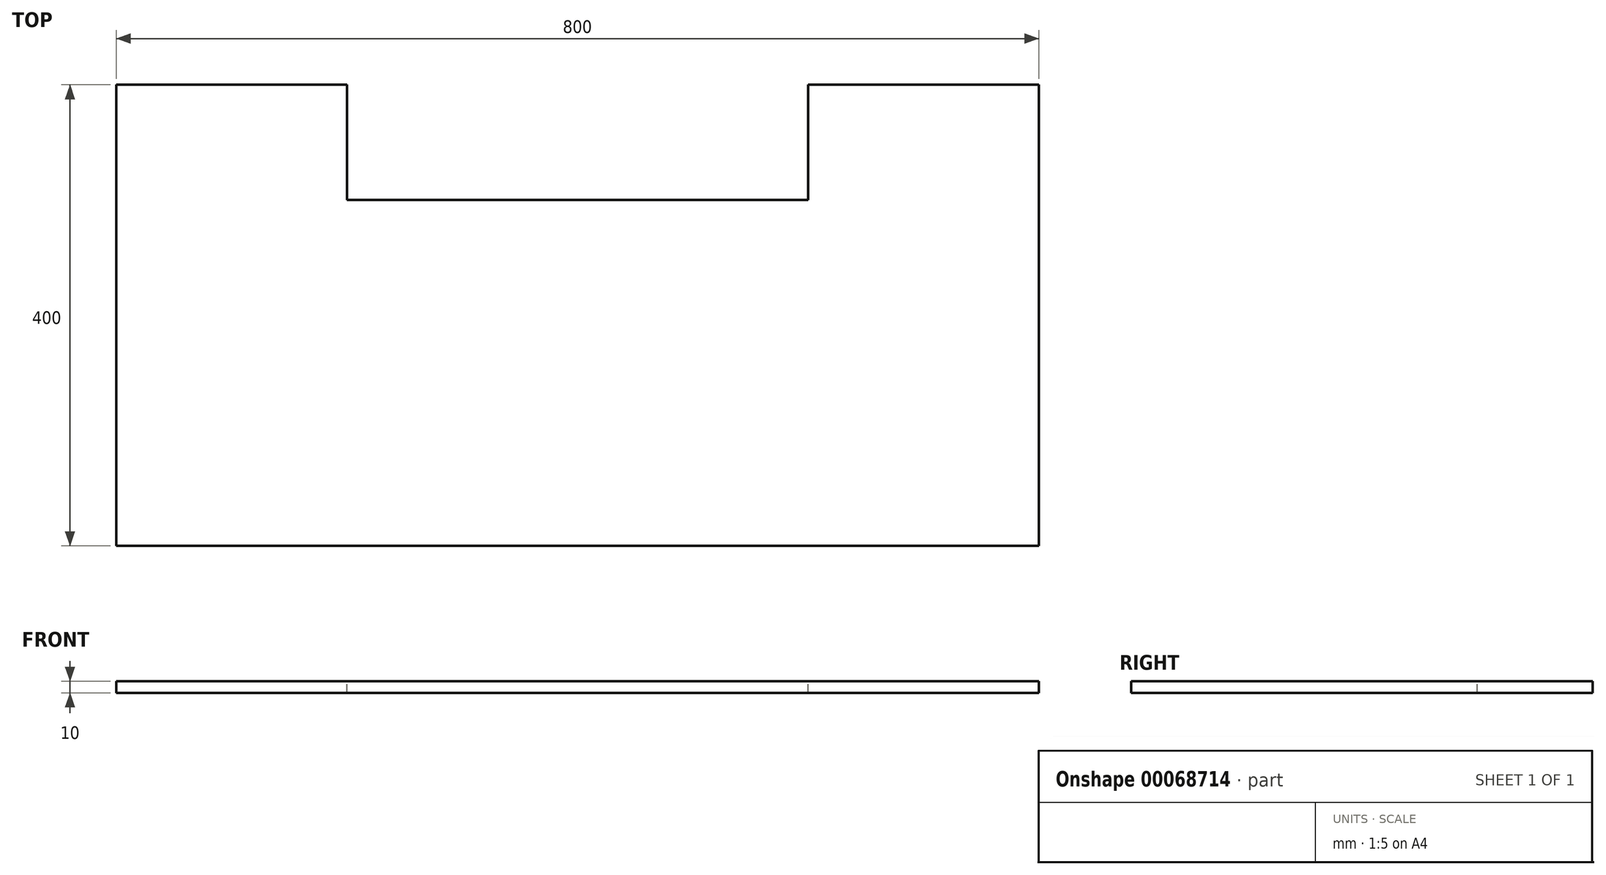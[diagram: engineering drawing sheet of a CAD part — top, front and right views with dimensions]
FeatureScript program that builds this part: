
annotation { "Feature Type Name" : "Feature", "Feature Type Description" : "" }
export const myFeature = defineFeature(function(context is Context, id is Id, definition is map)
    precondition{}
    {
        {
            var Q0;
            Q0=qCreatedBy(makeId("Top.planeOp"),FACE);
            var sketch = newSketch(context, id + "F0", { "sketchPlane" : qUnion([Q0])});
            skLineSegment(sketch, "E0.rect.bottom", {"start": v(400, 200) * mm, "end": v(-400, 200) * mm});
            skLineSegment(sketch, "E0.rect.top", {"start": v(400, -200) * mm, "end": v(-400, -200) * mm});
            skLineSegment(sketch, "E0.rect.left", {"start": v(400, 200) * mm, "end": v(400, -200) * mm});
            skLineSegment(sketch, "E0.rect.right", {"start": v(-400, 200) * mm, "end": v(-400, -200) * mm});
            skPoint(sketch, "E0.rect.middle", {"position": v(0, 0) * mm});
            skSolve(sketch);
        }
        {
            var Q0;
            Q0 = qSketchRegion(id + "F0", true);
            extrude(context, id + "F1", {"entities" : qUnion([Q0]), "depth" : 10 * mm});
        }
        {
            var Q0;
            Q0=makeQuery(id+"F1.opExtrude","CAP_FACE",FACE,{"disambiguationData":[OSD([sQuery(id+"F0.wireOp",EDGE,"E0.rect.bottom"),sQuery(id+"F0.wireOp",EDGE,"E0.rect.top"),sQuery(id+"F0.wireOp",EDGE,"E0.rect.left"),sQuery(id+"F0.wireOp",EDGE,"E0.rect.right")])],"isStart":false});
            var sketch = newSketch(context, id + "F2", { "sketchPlane" : qUnion([Q0])});
            skLineSegment(sketch, "E1.bottom", {"start": v(-200, 200) * mm, "end": v(200, 200) * mm});
            skLineSegment(sketch, "E1.top", {"start": v(-200, 100) * mm, "end": v(200, 100) * mm});
            skLineSegment(sketch, "E1.left", {"start": v(-200, 200) * mm, "end": v(-200, 100) * mm});
            skLineSegment(sketch, "E1.right", {"start": v(200, 200) * mm, "end": v(200, 100) * mm});
            skSolve(sketch);
        }
        {
            var Q0;
            Q0 = qSketchRegion(id + "F2", true);
            extrude(context, id + "F3", {"entities" : qUnion([Q0]), "operationType" : NewBodyOperationType.REMOVE, "endBound" : BoundingType.THROUGH_ALL, "oppositeDirection" : true, "depth" : 25 * mm});
        }
    });
